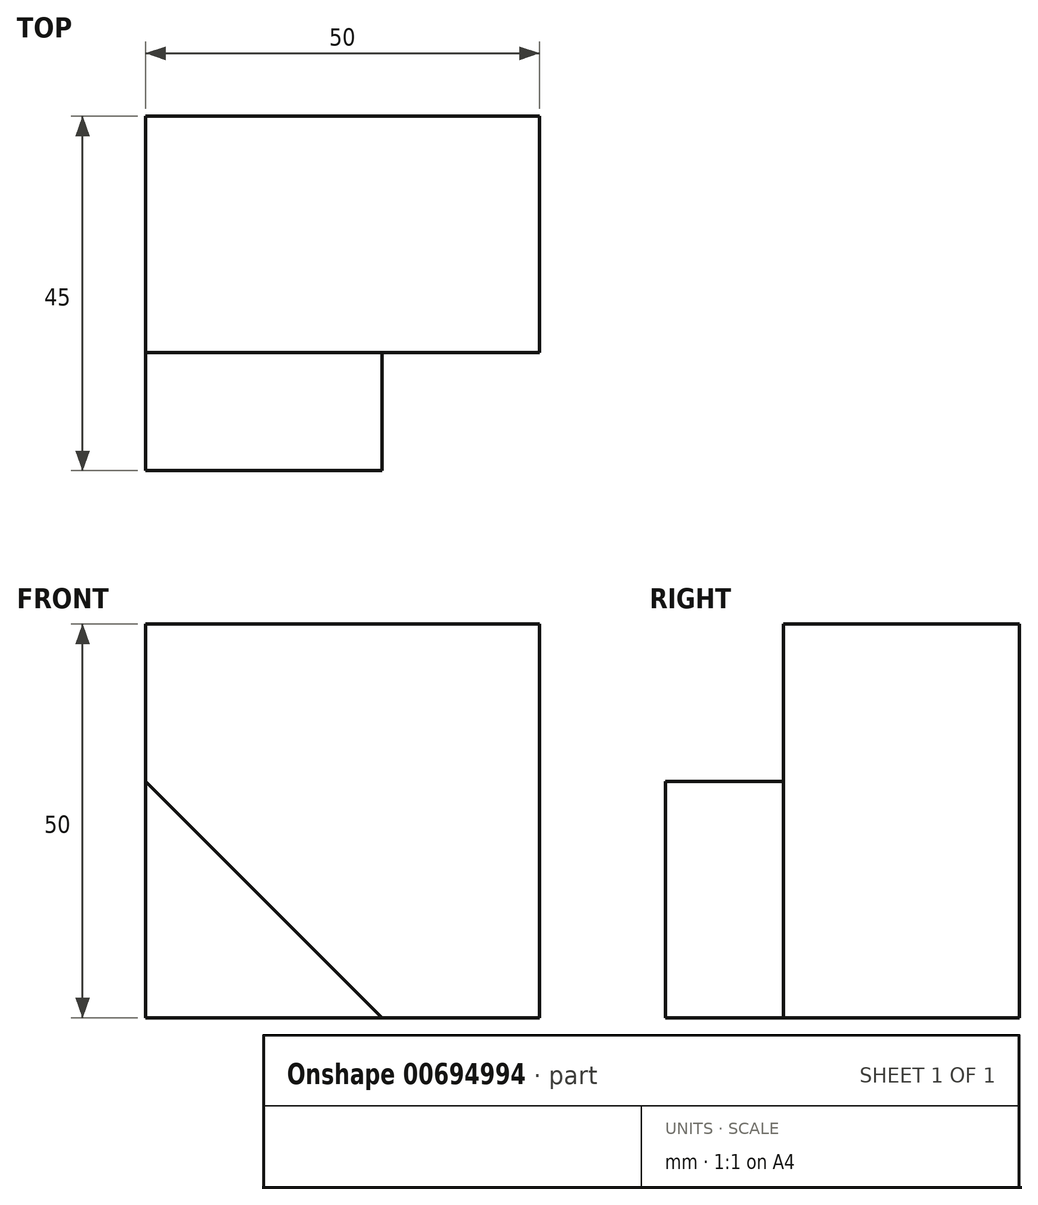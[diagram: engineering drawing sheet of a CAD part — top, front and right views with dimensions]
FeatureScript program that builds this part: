
annotation { "Feature Type Name" : "Feature", "Feature Type Description" : "" }
export const myFeature = defineFeature(function(context is Context, id is Id, definition is map)
    precondition{}
    {
        {
            var Q0;
            Q0=qCreatedBy(makeId("Front.planeOp"),FACE);
            var sketch = newSketch(context, id + "F0", { "sketchPlane" : qUnion([Q0])});
            skLineSegment(sketch, "E0", {"start": v(0, 0) * mm, "end": v(0, 30) * mm});
            skLineSegment(sketch, "E1", {"start": v(0, 0) * mm, "end": v(30, 0) * mm});
            skLineSegment(sketch, "E2", {"start": v(30, 0) * mm, "end": v(0, 30) * mm});
            skSolve(sketch);
        }
        {
            var Q0;
            Q0 = qSketchRegion(id + "F0", true);
            extrude(context, id + "F1", {"entities" : qUnion([Q0]), "oppositeDirection" : true, "depth" : 15 * mm, "offsetDistance" : 25 * mm});
        }
        {
            var Q0;
            Q0=qCreatedBy(makeId("Front.planeOp"),FACE);
            cPlane(context, id + "F2", {"entities" : qUnion([Q0]), "cplaneType" : CPlaneType.OFFSET, "offset" : 15 * mm, "oppositeDirection" : true, "width" : 150 * mm, "height" : 150 * mm});
        }
        {
            var Q0;
            Q0=qCreatedBy(id+"F2.planeOp",FACE);
            var sketch = newSketch(context, id + "F3", { "sketchPlane" : qUnion([Q0])});
            skLineSegment(sketch, "E3.bottom", {"start": v(0, 0) * mm, "end": v(50, 0) * mm});
            skLineSegment(sketch, "E3.top", {"start": v(0, 50) * mm, "end": v(50, 50) * mm});
            skLineSegment(sketch, "E3.left", {"start": v(0, 0) * mm, "end": v(0, 50) * mm});
            skLineSegment(sketch, "E3.right", {"start": v(50, 0) * mm, "end": v(50, 50) * mm});
            skSolve(sketch);
        }
        {
            var Q0;
            Q0 = qSketchRegion(id + "F3", true);
            extrude(context, id + "F4", {"entities" : qUnion([Q0]), "operationType" : NewBodyOperationType.ADD, "oppositeDirection" : true, "depth" : 30 * mm, "offsetDistance" : 25 * mm});
        }
        {
            var Q0;
            Q0=makeQuery(id+"F4.opExtrude","SWEPT_FACE",FACE,{"disambiguationData":[OSD([sQuery(id+"F3.wireOp",EDGE,"E3.top")])]});
            var sketch = newSketch(context, id + "F5", { "sketchPlane" : qUnion([Q0])});
            skCircle(sketch, "E4", {"center": v(15, 30) * mm, "radius": 5 * mm});
            skPoint(sketch, "E4.centerSnap0", {"position": v(0, 30) * mm});
            skSolve(sketch);
        }
        {
            var Q0;
            Q0=makeQuery(id+"F5.imprint","IMPRINT",FACE,{"disambiguationData":[TD([[makeQuery(id+"F5.imprint","IMPRINT",EDGE,{"derivedFrom":sQuery(id+"F5.wireOp",EDGE,"E4")}),1.0]])]});
            var Q1;
            Q1=sQuery(id+"F5.wireOp",EDGE,"E4");
            extrude(context, id + "F6", {"entities" : qUnion([Q0]), "operationType" : NewBodyOperationType.ADD, "surfaceEntities" : qUnion([Q1]), "endBound" : BoundingType.UP_TO_NEXT, "oppositeDirection" : true, "depth" : 25 * mm, "offsetDistance" : 25 * mm});
        }
    });
